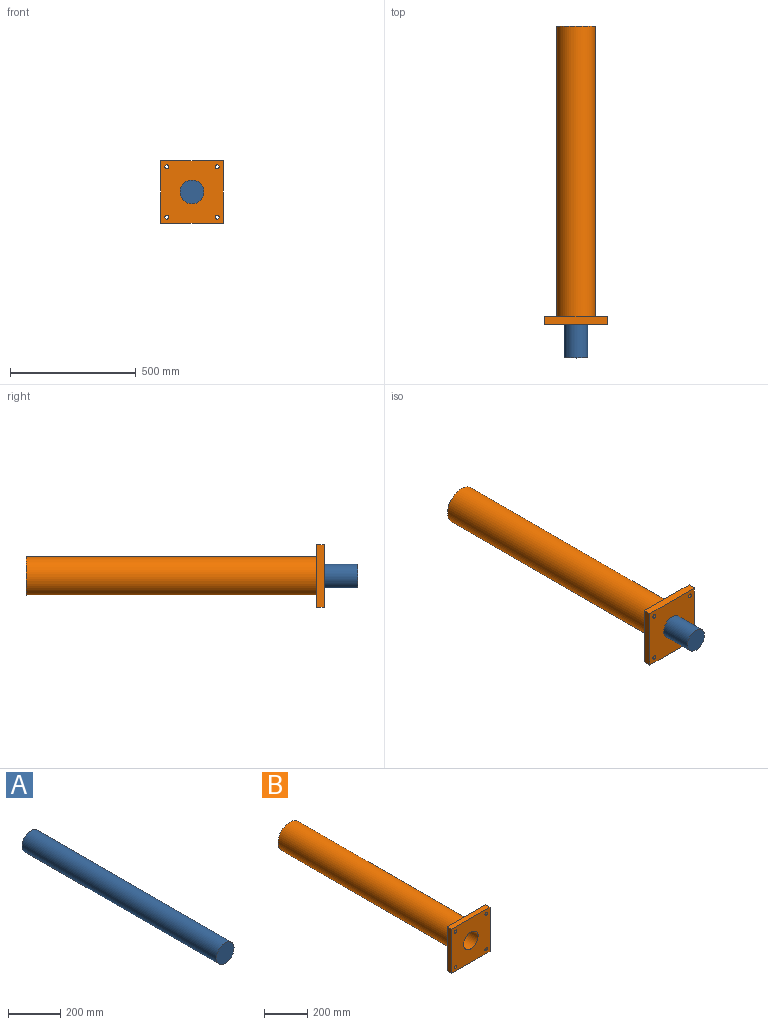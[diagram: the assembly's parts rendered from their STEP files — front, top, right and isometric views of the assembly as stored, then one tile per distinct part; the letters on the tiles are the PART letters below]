
ASSEMBLY  parts=2 mates=1
PART A: 3 faces, bbox 95x1050x95 mm
  f0: cylinder r=47.5mm len=1050mm, axis (0,-1,0), area 313373.9mm2, adj f1,f2
  f1: plane 95x95mm, normal (0,1,0), area 7088.2mm2, adj f0
  f2: plane 95x95mm, normal (0,-1,0), area 7088.2mm2, adj f0
PART B: 14 faces, bbox 250x1185x250 mm
  f0: plane 250x30mm, normal (0,0,-1), area 7500mm2, adj f1,f3,f4,f5
  f1: plane 250x30mm, normal (1,0,0), area 7500mm2, adj f0,f2,f4,f5
  f2: plane 250x30mm, normal (0,0,1), area 7500mm2, adj f1,f3,f4,f5
  f3: plane 250x30mm, normal (-1,0,0), area 7500mm2, adj f0,f2,f4,f5
  f4: plane 250x250mm, normal (0,-1,0), area 54607.5mm2, adj f0,f1,f2,f3,f8,f10,f11,f12
  f5: plane 250x250mm, normal (0,1,0), area 42826.6mm2, adj f0,f1,f2,f3,f6,f10,f11,f12
  f6: cylinder r=77.5mm len=1155mm, axis (0,-1,0), area 562423.6mm2, adj f5,f7
  f7: plane 155x155mm, normal (0,1,0), area 18869.2mm2, adj f6
  f8: cylinder r=47.5mm len=1100mm, axis (0,-1,0), area 328296.4mm2, adj f4,f9
  f9: plane 95x95mm, normal (0,-1,0), area 7088.2mm2, adj f8
  f10: cylinder r=8mm len=30mm, axis (0,-1,0), area 1508mm2, adj f4,f5
  f11: cylinder r=8mm len=30mm, axis (0,-1,0), area 1508mm2, adj f4,f5
  f12: cylinder r=8mm len=30mm, axis (0,-1,0), area 1508mm2, adj f4,f5
  f13: cylinder r=8mm len=30mm, axis (0,-1,0), area 1508mm2, adj f4,f5
PLACE A t=(186.1,-537.1,449.49)mm
PLACE B t=(188.53,-372.96,449.49)mm fixed
MATE slider A.f0 <-> B.f8  axis (0,1,0) through (188.53,512.9,449.49)mm
